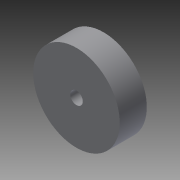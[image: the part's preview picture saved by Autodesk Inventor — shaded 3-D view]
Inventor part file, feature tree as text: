
AUTODESK INVENTOR PART (.ipt)
format: ipt  version: 2013 (Build 170138000, 138)  size: 74,240 bytes
history: native  units: mm
features: extrude x1, sketch x1
ambient origin geometry x8: Origin, YZ Plane, XZ Plane, XY Plane, X Axis, Y Axis, Z Axis, Center Point
bodies: Solid1 (feature_tree)
feature tree (2):
  extrude  "Extrusion1"  Depth=19.2mm
  sketch  "Sketch1"  dims[d0=2.8mm d2=19.2mm d3=6.0mm d4=0.0mm]
